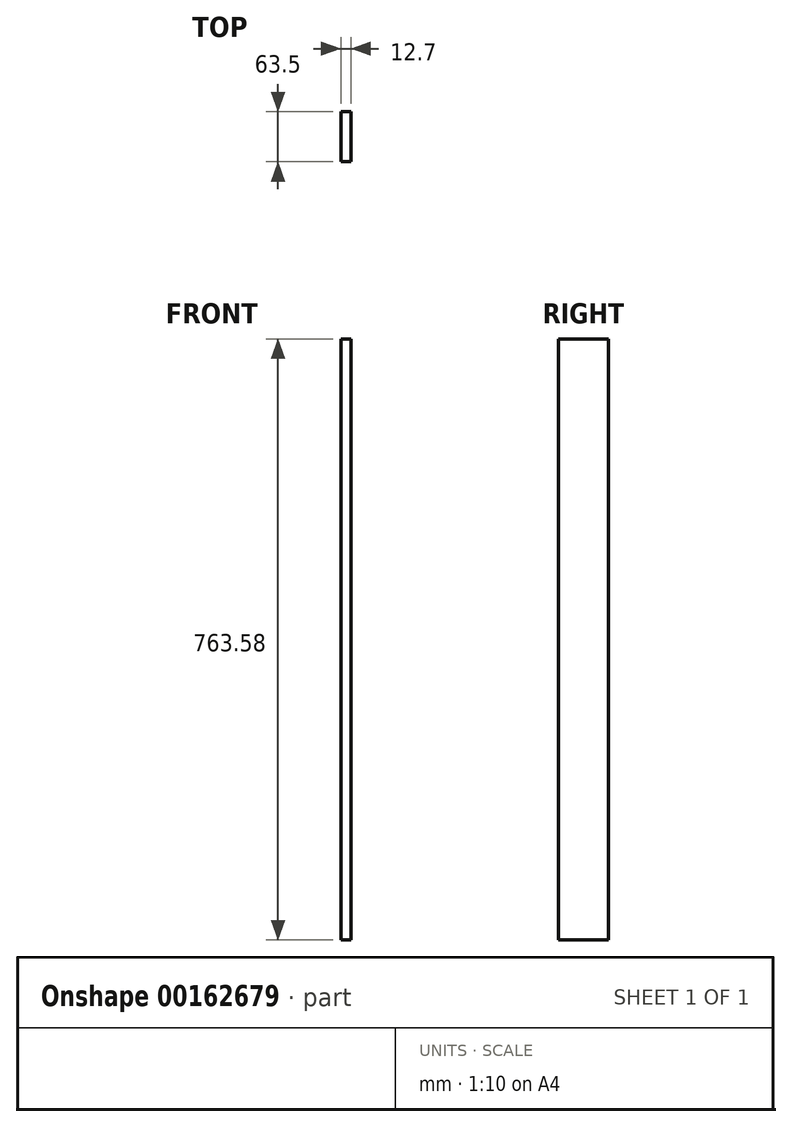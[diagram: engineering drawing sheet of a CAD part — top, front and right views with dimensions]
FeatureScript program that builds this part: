
annotation { "Feature Type Name" : "Feature", "Feature Type Description" : "" }
export const myFeature = defineFeature(function(context is Context, id is Id, definition is map)
    precondition{}
    {
        {
            var Q0;
            Q0=qCreatedBy(makeId("Right.planeOp"),FACE);
            var sketch = newSketch(context, id + "F0", { "sketchPlane" : qUnion([Q0])});
            skLineSegment(sketch, "E0.bottom", {"start": v(-43.96, 438.7) * mm, "end": v(19.54, 438.7) * mm});
            skLineSegment(sketch, "E0.top", {"start": v(-43.96, -324.9) * mm, "end": v(19.54, -324.9) * mm});
            skLineSegment(sketch, "E0.left", {"start": v(-43.96, 438.7) * mm, "end": v(-43.96, -324.9) * mm});
            skLineSegment(sketch, "E0.right", {"start": v(19.54, 438.7) * mm, "end": v(19.54, -324.9) * mm});
            skSolve(sketch);
        }
        {
            var Q0;
            Q0 = qSketchRegion(id + "F0", true);
            extrude(context, id + "F1", {"entities" : qUnion([Q0]), "depth" : 12.7 * mm});
        }
    });
